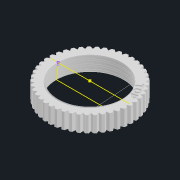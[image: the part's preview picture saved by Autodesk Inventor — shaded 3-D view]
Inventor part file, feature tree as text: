
AUTODESK INVENTOR PART (.ipt)
format: ipt  version: 2021.3 (Build 253353000, 353)  size: 597,504 bytes
history: native  units: mm
features: sketch x5, extrude x3, helix x2, draft x1, pattern_circular x1, projected_geometry x1
ambient origin geometry x8: Origin, YZ Plane, XZ Plane, XY Plane, X Axis, Y Axis, Z Axis, Center Point
bodies: Solid1 (feature_tree)
feature tree (13):
  extrude  "Extrusion1"  Depth=6.52mm TaperAngle=0.0deg
  draft  "FaceDraft1"
  sketch  "Sketch2"  dims[d7=2.0mm d8=9.0mm d9=10.0mm d10=1.047198mm d11=90.0deg d12=90.0deg d13=0.0mm d14=0.0mm d15=2.0mm d16=3.0mm d17=10.0mm d18=-1.047198mm d19=90.0deg d20=90.0deg d21=0.0mm d22=0.0mm d23=3.0mm d92=3.0mm]
  sketch  "Sketch4"  dims[d94=10.0mm d95=0.0mm d96=450.0mm d97=360.0deg]
  helix  "Coil1"  [1 undecoded]
  helix  "Coil2"  [1 undecoded]
  extrude  "Extrusion2"  Depth=450.0mm TaperAngle=360.0deg
  pattern_circular  "Circular Pattern3"  Angle=30.0deg  [1 undecoded]
  extrude  "Extrusion3"  Depth=0.4mm TaperAngle=0.0deg
  sketch  "Sketch1"  dims[d0=26.5mm d2=6.52mm d3=0.0mm d4=1.047198mm]
  sketch  "Sketch9"  dims[d99=1.2mm]
  sketch  "Sketch10"  dims[d100=30.0deg d101=30.0deg d102=0.4mm d103=0.0mm]
  projected_geometry  "Projected Loop1"
note: 3 required parameter values undecoded (feature->parameter linkage not recoverable at this tier; creation-order binding heuristic only, values carry confidence <= 0.55)
